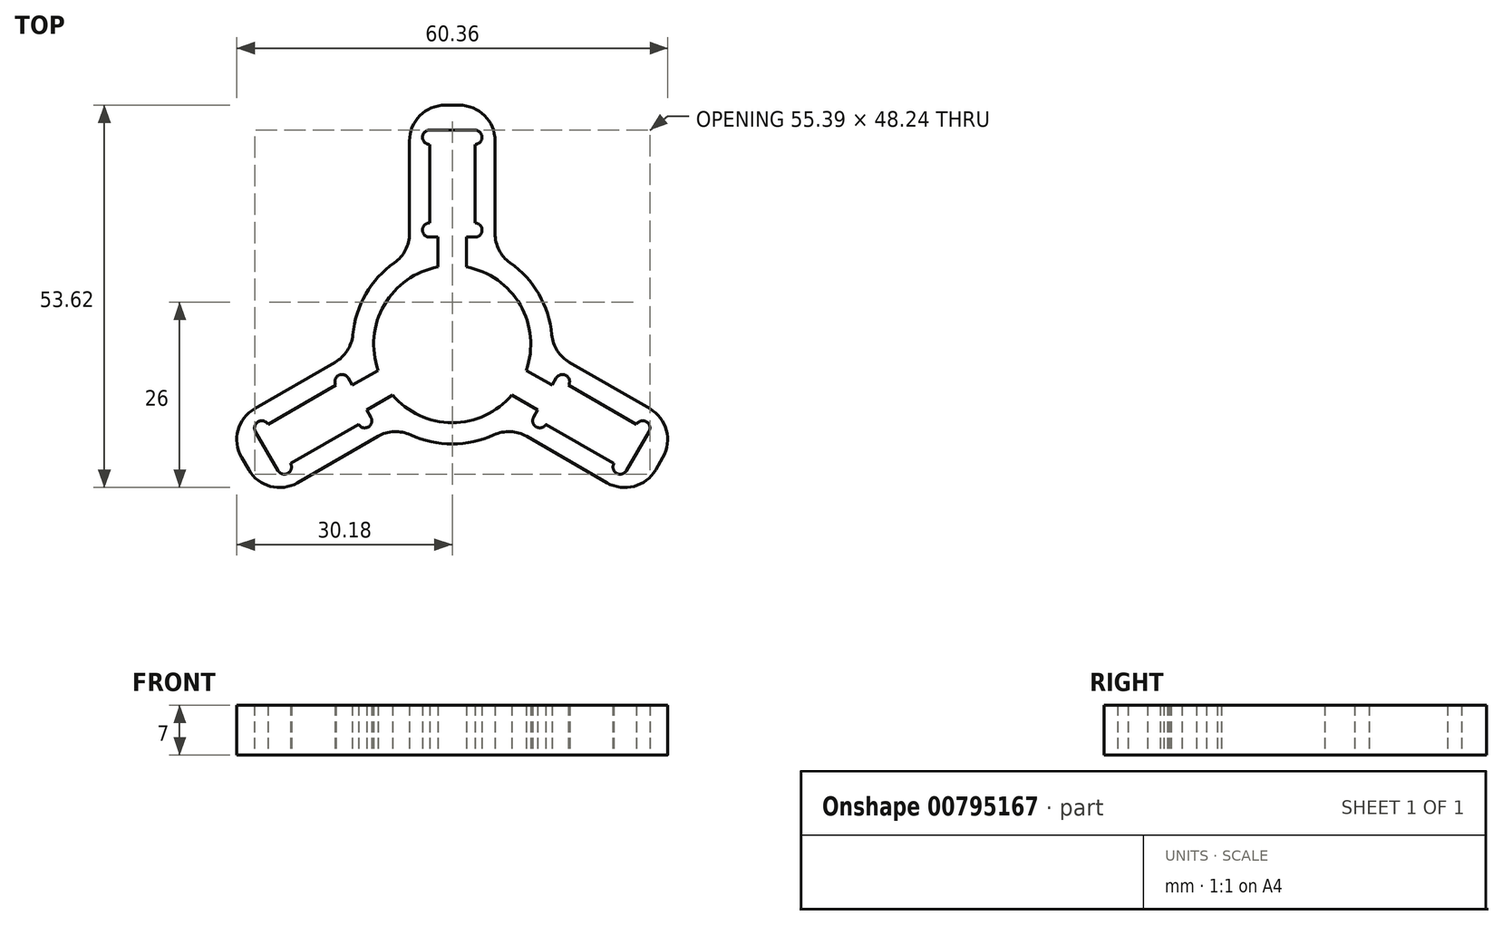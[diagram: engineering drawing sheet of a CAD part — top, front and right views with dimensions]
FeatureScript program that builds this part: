
annotation { "Feature Type Name" : "Feature", "Feature Type Description" : "" }
export const myFeature = defineFeature(function(context is Context, id is Id, definition is map)
    precondition{}
    {
        {
            var Q0;
            Q0=qCreatedBy(makeId("Top.planeOp"),FACE);
            var sketch = newSketch(context, id + "F0", { "sketchPlane" : qUnion([Q0])});
            skArc(sketch, "E0", {"start": v(-2, 10.82) * mm, "mid": v(-9.53, 5.5) * mm, "end": v(-10.37, -3.68) * mm});
            skArc(sketch, "E1", {"start": v(-8.1, 11.42) * mm, "mid": v(-12.12, 7) * mm, "end": v(-13.94, 1.31) * mm});
            skLineSegment(sketch, "E2.left", {"start": v(2, 10.82) * mm, "end": v(2, 15) * mm});
            skLineSegment(sketch, "E2.right", {"start": v(-2, 10.82) * mm, "end": v(-2, 15) * mm});
            skPoint(sketch, "E2.middle", {"position": v(0, 15) * mm});
            skLineSegment(sketch, "E3.bottom", {"start": v(3.17, 15) * mm, "end": v(2, 15) * mm});
            skLineSegment(sketch, "E3.top", {"start": v(3.18, 30) * mm, "end": v(-3.17, 30) * mm});
            skPoint(sketch, "E3.middle", {"position": v(0, 22.5) * mm});
            skPoint(sketch, "E2.bottom.end.orphan", {"position": v(-2, 2.5) * mm});
            skPoint(sketch, "E2.bottom.start.orphan", {"position": v(2, 2.5) * mm});
            skPoint(sketch, "E2.top.end.orphan", {"position": v(-2, 27.5) * mm});
            skPoint(sketch, "E2.top.start.orphan", {"position": v(2, 27.5) * mm});
            skLineSegment(sketch, "E4.trimOffspring", {"start": v(-2, 15) * mm, "end": v(-3.18, 15) * mm});
            skLineSegment(sketch, "E5.top", {"start": v(1, 33.5) * mm, "end": v(-1, 33.5) * mm});
            skLineSegment(sketch, "E5.left", {"start": v(6, 15.5) * mm, "end": v(6, 28.5) * mm});
            skLineSegment(sketch, "E5.right", {"start": v(-6, 15.5) * mm, "end": v(-6, 28.5) * mm});
            skPoint(sketch, "E6.orphan", {"position": v(-6, 11.5) * mm});
            skPoint(sketch, "E7.orphan", {"position": v(6, 11.5) * mm});
            skLineSegment(sketch, "E8", {"start": v(-3.17, 29) * mm, "end": v(3.17, 29) * mm, "construction": true});
            skLineSegment(sketch, "E9", {"start": v(-3.18, 16) * mm, "end": v(3.17, 16) * mm, "construction": true});
            skArc(sketch, "E10", {"start": v(-3.18, 17) * mm, "mid": v(-4.18, 16) * mm, "end": v(-3.18, 15) * mm});
            skArc(sketch, "E11", {"start": v(3.17, 15) * mm, "mid": v(4.17, 16) * mm, "end": v(3.17, 17) * mm});
            skArc(sketch, "E12", {"start": v(3.17, 28) * mm, "mid": v(4.18, 29) * mm, "end": v(3.18, 30) * mm});
            skArc(sketch, "E13", {"start": v(-3.17, 30) * mm, "mid": v(-4.18, 29) * mm, "end": v(-3.17, 28) * mm});
            skLineSegment(sketch, "E14.trimOffspring", {"start": v(-3.18, 17) * mm, "end": v(-3.17, 28) * mm});
            skLineSegment(sketch, "E15.trimOffspring", {"start": v(3.17, 17) * mm, "end": v(3.17, 28) * mm});
            skPoint(sketch, "E16.visualSharp", {"position": v(-6, 12.65) * mm});
            skArc(sketch, "E16.filletArc", {"start": v(-8.1, 11.42) * mm, "mid": v(-6.56, 13.2) * mm, "end": v(-6, 15.5) * mm});
            skPoint(sketch, "E17.visualSharp", {"position": v(6, 12.65) * mm});
            skArc(sketch, "E17.filletArc", {"start": v(6, 15.5) * mm, "mid": v(6.56, 13.2) * mm, "end": v(8.1, 11.42) * mm});
            skPoint(sketch, "E18.visualSharp", {"position": v(-6, 33.5) * mm});
            skArc(sketch, "E18.filletArc", {"start": v(-1, 33.5) * mm, "mid": v(-4.54, 32.04) * mm, "end": v(-6, 28.5) * mm});
            skPoint(sketch, "E19.visualSharp", {"position": v(6, 33.5) * mm});
            skArc(sketch, "E19.filletArc", {"start": v(6, 28.5) * mm, "mid": v(4.54, 32.04) * mm, "end": v(1, 33.5) * mm});
            skLineSegment(sketch, "E20.1.0", {"start": v(-10.42, -12.94) * mm, "end": v(-21.68, -19.45) * mm});
            skPoint(sketch, "E20.1.1", {"position": v(-24.82, -12.02) * mm});
            skPoint(sketch, "E20.1.2", {"position": v(-12.96, -0.55) * mm});
            skLineSegment(sketch, "E20.1.3", {"start": v(-8.37, -7.14) * mm, "end": v(-12, -9.23) * mm});
            skPoint(sketch, "E20.1.4", {"position": v(-26.01, -21.95) * mm});
            skArc(sketch, "E20.1.5", {"start": v(-24.4, -17.75) * mm, "mid": v(-23.03, -18.12) * mm, "end": v(-22.66, -16.75) * mm});
            skLineSegment(sketch, "E20.1.6", {"start": v(-10.37, -3.68) * mm, "end": v(-14, -5.77) * mm});
            skLineSegment(sketch, "E20.1.7", {"start": v(-16.3, -5.75) * mm, "end": v(-25.84, -11.25) * mm});
            skLineSegment(sketch, "E20.1.8", {"start": v(-16.42, -2.55) * mm, "end": v(-27.68, -9.05) * mm});
            skLineSegment(sketch, "E20.1.9", {"start": v(-29.51, -15.88) * mm, "end": v(-28.51, -17.62) * mm});
            skPoint(sketch, "E20.1.10", {"position": v(-13.95, -1.13) * mm});
            skPoint(sketch, "E20.1.11", {"position": v(-19.49, -11.25) * mm});
            skLineSegment(sketch, "E20.1.12", {"start": v(-27.57, -12.25) * mm, "end": v(-24.4, -17.75) * mm});
            skPoint(sketch, "E20.1.13", {"position": v(-22.82, -15.48) * mm});
            skArc(sketch, "E20.1.14", {"start": v(-25.84, -11.25) * mm, "mid": v(-27.2, -10.88) * mm, "end": v(-27.57, -12.25) * mm});
            skArc(sketch, "E20.1.15", {"start": v(-14.58, -4.75) * mm, "mid": v(-15.94, -4.38) * mm, "end": v(-16.3, -5.75) * mm});
            skArc(sketch, "E20.1.16", {"start": v(-28.51, -17.62) * mm, "mid": v(-25.48, -19.95) * mm, "end": v(-21.68, -19.45) * mm});
            skLineSegment(sketch, "E20.1.17", {"start": v(-12.27, -10.75) * mm, "end": v(-15.44, -5.25) * mm, "construction": true});
            skArc(sketch, "E20.1.18", {"start": v(-13.13, -11.25) * mm, "mid": v(-11.77, -11.62) * mm, "end": v(-11.4, -10.25) * mm});
            skArc(sketch, "E20.1.19", {"start": v(-27.68, -9.05) * mm, "mid": v(-30.01, -12.09) * mm, "end": v(-29.51, -15.88) * mm});
            skLineSegment(sketch, "E20.1.20", {"start": v(-23.53, -17.25) * mm, "end": v(-26.7, -11.75) * mm, "construction": true});
            skPoint(sketch, "E20.1.21", {"position": v(-32.01, -11.55) * mm});
            skArc(sketch, "E20.1.22", {"start": v(-16.42, -2.55) * mm, "mid": v(-14.7, -0.92) * mm, "end": v(-13.94, 1.31) * mm});
            skPoint(sketch, "E20.1.23", {"position": v(-7.95, -11.52) * mm});
            skArc(sketch, "E20.1.24", {"start": v(-5.83, -12.73) * mm, "mid": v(-8.15, -12.28) * mm, "end": v(-10.42, -12.94) * mm});
            skPoint(sketch, "E20.1.25", {"position": v(-13, -7.5) * mm});
            skPoint(sketch, "E20.1.26", {"position": v(-6.96, -10.95) * mm});
            skLineSegment(sketch, "E20.1.27", {"start": v(-13.13, -11.25) * mm, "end": v(-22.66, -16.75) * mm});
            skPoint(sketch, "E20.1.28", {"position": v(-19.49, -11.25) * mm});
            skLineSegment(sketch, "E20.1.29", {"start": v(-12, -9.23) * mm, "end": v(-11.4, -10.25) * mm});
            skLineSegment(sketch, "E20.1.30", {"start": v(-14.58, -4.75) * mm, "end": v(-14, -5.77) * mm});
            skLineSegment(sketch, "E20.2.0", {"start": v(16.42, -2.55) * mm, "end": v(27.68, -9.05) * mm});
            skPoint(sketch, "E20.2.1", {"position": v(22.82, -15.48) * mm});
            skPoint(sketch, "E20.2.2", {"position": v(6.96, -10.95) * mm});
            skLineSegment(sketch, "E20.2.3", {"start": v(10.37, -3.68) * mm, "end": v(14, -5.77) * mm});
            skPoint(sketch, "E20.2.4", {"position": v(32.01, -11.55) * mm});
            skArc(sketch, "E20.2.5", {"start": v(27.57, -12.25) * mm, "mid": v(27.2, -10.88) * mm, "end": v(25.84, -11.25) * mm});
            skLineSegment(sketch, "E20.2.6", {"start": v(8.37, -7.14) * mm, "end": v(12, -9.23) * mm});
            skLineSegment(sketch, "E20.2.7", {"start": v(13.13, -11.25) * mm, "end": v(22.66, -16.75) * mm});
            skLineSegment(sketch, "E20.2.8", {"start": v(10.42, -12.94) * mm, "end": v(21.68, -19.45) * mm});
            skLineSegment(sketch, "E20.2.9", {"start": v(28.51, -17.62) * mm, "end": v(29.51, -15.88) * mm});
            skPoint(sketch, "E20.2.10", {"position": v(7.95, -11.52) * mm});
            skPoint(sketch, "E20.2.11", {"position": v(19.49, -11.25) * mm});
            skLineSegment(sketch, "E20.2.12", {"start": v(24.4, -17.75) * mm, "end": v(27.57, -12.25) * mm});
            skPoint(sketch, "E20.2.13", {"position": v(24.82, -12.02) * mm});
            skArc(sketch, "E20.2.14", {"start": v(22.66, -16.75) * mm, "mid": v(23.03, -18.12) * mm, "end": v(24.4, -17.75) * mm});
            skArc(sketch, "E20.2.15", {"start": v(11.4, -10.25) * mm, "mid": v(11.77, -11.62) * mm, "end": v(13.13, -11.25) * mm});
            skArc(sketch, "E20.2.16", {"start": v(29.51, -15.88) * mm, "mid": v(30.01, -12.09) * mm, "end": v(27.68, -9.05) * mm});
            skLineSegment(sketch, "E20.2.17", {"start": v(15.44, -5.25) * mm, "end": v(12.27, -10.75) * mm, "construction": true});
            skArc(sketch, "E20.2.18", {"start": v(16.3, -5.75) * mm, "mid": v(15.94, -4.38) * mm, "end": v(14.58, -4.75) * mm});
            skArc(sketch, "E20.2.19", {"start": v(21.68, -19.45) * mm, "mid": v(25.48, -19.95) * mm, "end": v(28.51, -17.62) * mm});
            skLineSegment(sketch, "E20.2.20", {"start": v(26.7, -11.75) * mm, "end": v(23.53, -17.25) * mm, "construction": true});
            skPoint(sketch, "E20.2.21", {"position": v(26.01, -21.95) * mm});
            skArc(sketch, "E20.2.22", {"start": v(10.42, -12.94) * mm, "mid": v(8.15, -12.28) * mm, "end": v(5.83, -12.73) * mm});
            skPoint(sketch, "E20.2.23", {"position": v(13.95, -1.13) * mm});
            skArc(sketch, "E20.2.24", {"start": v(13.94, 1.31) * mm, "mid": v(14.7, -0.92) * mm, "end": v(16.42, -2.55) * mm});
            skPoint(sketch, "E20.2.25", {"position": v(13, -7.5) * mm});
            skPoint(sketch, "E20.2.26", {"position": v(12.96, -0.55) * mm});
            skLineSegment(sketch, "E20.2.27", {"start": v(16.3, -5.75) * mm, "end": v(25.84, -11.25) * mm});
            skPoint(sketch, "E20.2.28", {"position": v(19.49, -11.25) * mm});
            skLineSegment(sketch, "E20.2.29", {"start": v(14, -5.77) * mm, "end": v(14.58, -4.75) * mm});
            skLineSegment(sketch, "E20.2.30", {"start": v(11.4, -10.25) * mm, "end": v(12, -9.23) * mm});
            skArc(sketch, "E21.trimOffspring", {"start": v(13.94, 1.31) * mm, "mid": v(12.12, 7) * mm, "end": v(8.1, 11.42) * mm});
            skArc(sketch, "E22.trimOffspring", {"start": v(10.37, -3.68) * mm, "mid": v(9.53, 5.5) * mm, "end": v(2, 10.82) * mm});
            skArc(sketch, "E23.trimOffspring", {"start": v(-5.83, -12.73) * mm, "mid": v(0, -14) * mm, "end": v(5.83, -12.73) * mm});
            skArc(sketch, "E24.trimOffspring", {"start": v(-8.37, -7.14) * mm, "mid": v(0, -11) * mm, "end": v(8.37, -7.14) * mm});
            skSolve(sketch);
        }
        {
            var Q0;
            Q0=makeQuery(id+"F0.imprint","IMPRINT",FACE,{"disambiguationData":[TD([[makeQuery(id+"F0.imprint","IMPRINT",EDGE,{"derivedFrom":sQuery(id+"F0.wireOp",EDGE,"E0")}),-1.0]])]});
            extrude(context, id + "F1", {"entities" : qUnion([Q0]), "depth" : 7 * mm, "offsetDistance" : 25 * mm});
        }
    });
